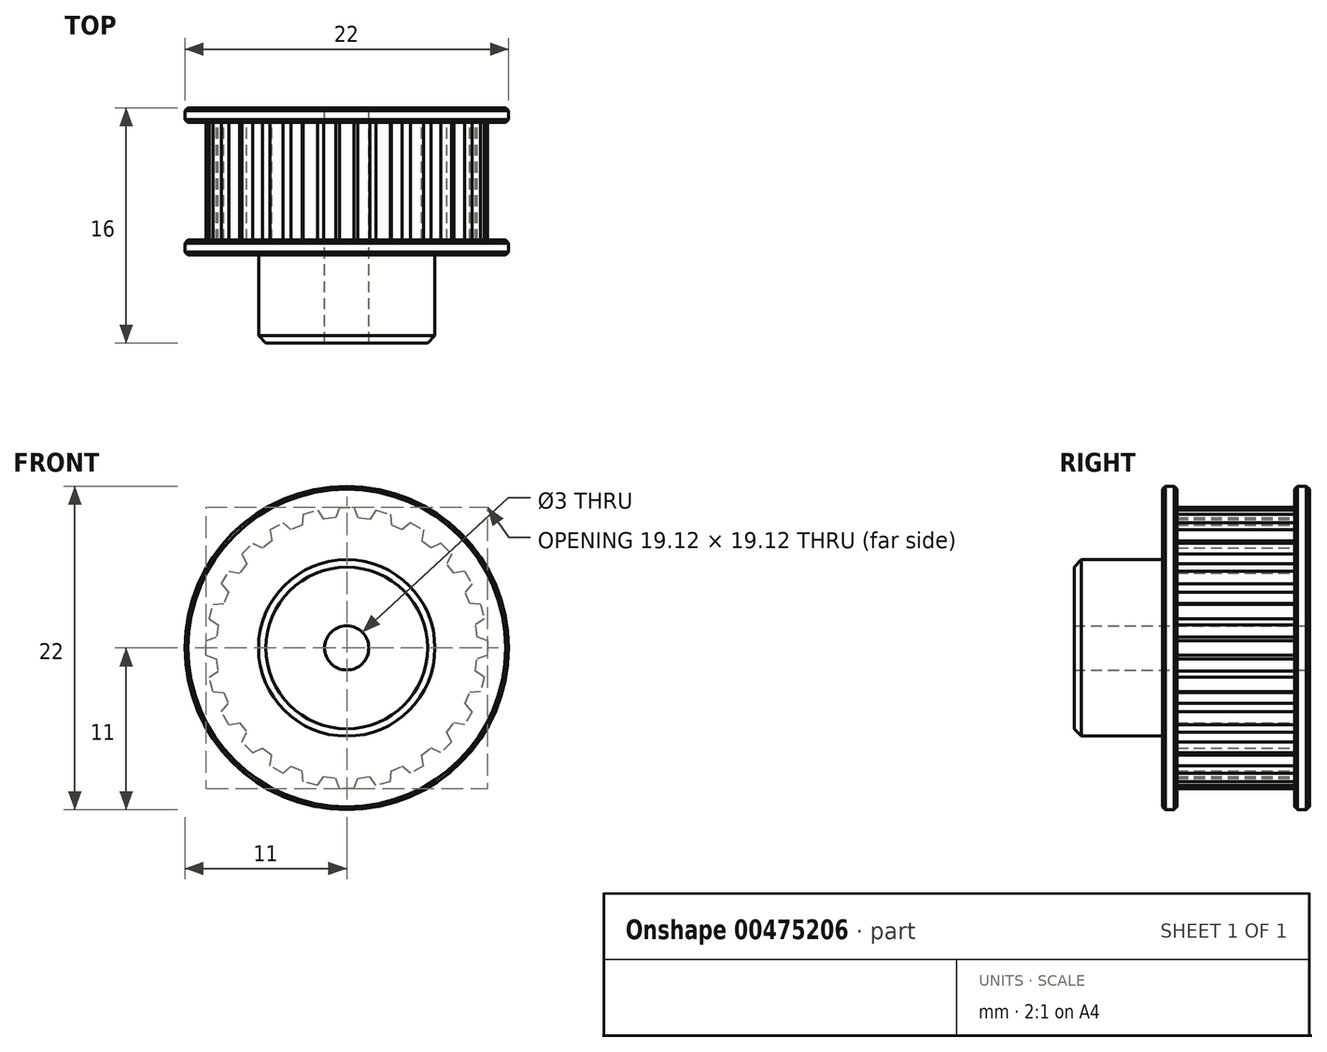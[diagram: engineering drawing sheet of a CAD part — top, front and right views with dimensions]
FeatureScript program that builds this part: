
annotation { "Feature Type Name" : "Feature", "Feature Type Description" : "" }
export const myFeature = defineFeature(function(context is Context, id is Id, definition is map)
    precondition{}
    {
        {
            var Q0;
            Q0=qCreatedBy(makeId("Front.planeOp"),FACE);
            var sketch = newSketch(context, id + "F0", { "sketchPlane" : qUnion([Q0])});
            skCircle(sketch, "E0", {"center": v(0, 0) * mm, "radius": 9.57 * mm, "construction": true});
            skCircle(sketch, "E1", {"center": v(0, 0) * mm, "radius": 6 * mm});
            skLineSegment(sketch, "E2", {"start": v(0, 9.56) * mm, "end": v(-0.5, 9.56) * mm});
            skLineSegment(sketch, "E3", {"start": v(-0.5, 9.56) * mm, "end": v(-0.75, 8.86) * mm});
            skLineSegment(sketch, "E4", {"start": v(-0.75, 8.86) * mm, "end": v(0, 8.86) * mm});
            skLineSegment(sketch, "E5.MirrorCS", {"start": v(0.75, 8.86) * mm, "end": v(0, 8.86) * mm});
            skLineSegment(sketch, "E6.MirrorCS", {"start": v(0, 9.56) * mm, "end": v(0.5, 9.56) * mm});
            skLineSegment(sketch, "E7.MirrorCS", {"start": v(0.5, 9.56) * mm, "end": v(0.75, 8.86) * mm});
            skLineSegment(sketch, "E8.1.0", {"start": v(1.56, 8.76) * mm, "end": v(2.3, 8.56) * mm});
            skLineSegment(sketch, "E8.1.1", {"start": v(3.02, 8.36) * mm, "end": v(2.3, 8.56) * mm});
            skLineSegment(sketch, "E8.1.2", {"start": v(2.96, 9.1) * mm, "end": v(3.02, 8.36) * mm});
            skLineSegment(sketch, "E8.1.3", {"start": v(2, 9.37) * mm, "end": v(1.56, 8.76) * mm});
            skLineSegment(sketch, "E8.1.4", {"start": v(2.47, 9.24) * mm, "end": v(2.96, 9.1) * mm});
            skLineSegment(sketch, "E8.1.5", {"start": v(2.47, 9.24) * mm, "end": v(2, 9.37) * mm});
            skLineSegment(sketch, "E8.2.0", {"start": v(3.78, 8.05) * mm, "end": v(4.43, 7.67) * mm});
            skLineSegment(sketch, "E8.2.1", {"start": v(5.08, 7.3) * mm, "end": v(4.43, 7.67) * mm});
            skLineSegment(sketch, "E8.2.2", {"start": v(5.21, 8.03) * mm, "end": v(5.08, 7.3) * mm});
            skLineSegment(sketch, "E8.2.3", {"start": v(4.35, 8.53) * mm, "end": v(3.78, 8.05) * mm});
            skLineSegment(sketch, "E8.2.4", {"start": v(4.78, 8.28) * mm, "end": v(5.21, 8.03) * mm});
            skLineSegment(sketch, "E8.2.5", {"start": v(4.78, 8.28) * mm, "end": v(4.35, 8.53) * mm});
            skLineSegment(sketch, "E8.3.0", {"start": v(5.73, 6.8) * mm, "end": v(6.27, 6.27) * mm});
            skLineSegment(sketch, "E8.3.1", {"start": v(6.8, 5.73) * mm, "end": v(6.27, 6.27) * mm});
            skLineSegment(sketch, "E8.3.2", {"start": v(7.11, 6.4) * mm, "end": v(6.8, 5.73) * mm});
            skLineSegment(sketch, "E8.3.3", {"start": v(6.4, 7.11) * mm, "end": v(5.73, 6.8) * mm});
            skLineSegment(sketch, "E8.3.4", {"start": v(6.76, 6.76) * mm, "end": v(7.11, 6.4) * mm});
            skLineSegment(sketch, "E8.3.5", {"start": v(6.76, 6.76) * mm, "end": v(6.4, 7.11) * mm});
            skLineSegment(sketch, "E8.4.0", {"start": v(7.3, 5.08) * mm, "end": v(7.67, 4.43) * mm});
            skLineSegment(sketch, "E8.4.1", {"start": v(8.05, 3.78) * mm, "end": v(7.67, 4.43) * mm});
            skLineSegment(sketch, "E8.4.2", {"start": v(8.53, 4.35) * mm, "end": v(8.05, 3.78) * mm});
            skLineSegment(sketch, "E8.4.3", {"start": v(8.03, 5.21) * mm, "end": v(7.3, 5.08) * mm});
            skLineSegment(sketch, "E8.4.4", {"start": v(8.28, 4.78) * mm, "end": v(8.53, 4.35) * mm});
            skLineSegment(sketch, "E8.4.5", {"start": v(8.28, 4.78) * mm, "end": v(8.03, 5.21) * mm});
            skLineSegment(sketch, "E8.5.0", {"start": v(8.36, 3.02) * mm, "end": v(8.56, 2.3) * mm});
            skLineSegment(sketch, "E8.5.1", {"start": v(8.76, 1.56) * mm, "end": v(8.56, 2.3) * mm});
            skLineSegment(sketch, "E8.5.2", {"start": v(9.37, 2) * mm, "end": v(8.76, 1.56) * mm});
            skLineSegment(sketch, "E8.5.3", {"start": v(9.1, 2.96) * mm, "end": v(8.36, 3.02) * mm});
            skLineSegment(sketch, "E8.5.4", {"start": v(9.24, 2.47) * mm, "end": v(9.37, 2) * mm});
            skLineSegment(sketch, "E8.5.5", {"start": v(9.24, 2.47) * mm, "end": v(9.1, 2.96) * mm});
            skLineSegment(sketch, "E8.6.0", {"start": v(8.86, 0.75) * mm, "end": v(8.86, 0) * mm});
            skLineSegment(sketch, "E8.6.1", {"start": v(8.86, -0.75) * mm, "end": v(8.86, 0) * mm});
            skLineSegment(sketch, "E8.6.2", {"start": v(9.56, -0.5) * mm, "end": v(8.86, -0.75) * mm});
            skLineSegment(sketch, "E8.6.3", {"start": v(9.56, 0.5) * mm, "end": v(8.86, 0.75) * mm});
            skLineSegment(sketch, "E8.6.4", {"start": v(9.56, 0) * mm, "end": v(9.56, -0.5) * mm});
            skLineSegment(sketch, "E8.6.5", {"start": v(9.56, 0) * mm, "end": v(9.56, 0.5) * mm});
            skLineSegment(sketch, "E8.7.0", {"start": v(8.76, -1.56) * mm, "end": v(8.56, -2.3) * mm});
            skLineSegment(sketch, "E8.7.1", {"start": v(8.36, -3.02) * mm, "end": v(8.56, -2.3) * mm});
            skLineSegment(sketch, "E8.7.2", {"start": v(9.1, -2.96) * mm, "end": v(8.36, -3.02) * mm});
            skLineSegment(sketch, "E8.7.3", {"start": v(9.37, -2) * mm, "end": v(8.76, -1.56) * mm});
            skLineSegment(sketch, "E8.7.4", {"start": v(9.24, -2.47) * mm, "end": v(9.1, -2.96) * mm});
            skLineSegment(sketch, "E8.7.5", {"start": v(9.24, -2.47) * mm, "end": v(9.37, -2) * mm});
            skLineSegment(sketch, "E8.8.0", {"start": v(8.05, -3.78) * mm, "end": v(7.67, -4.43) * mm});
            skLineSegment(sketch, "E8.8.1", {"start": v(7.3, -5.08) * mm, "end": v(7.67, -4.43) * mm});
            skLineSegment(sketch, "E8.8.2", {"start": v(8.03, -5.21) * mm, "end": v(7.3, -5.08) * mm});
            skLineSegment(sketch, "E8.8.3", {"start": v(8.53, -4.35) * mm, "end": v(8.05, -3.78) * mm});
            skLineSegment(sketch, "E8.8.4", {"start": v(8.28, -4.78) * mm, "end": v(8.03, -5.21) * mm});
            skLineSegment(sketch, "E8.8.5", {"start": v(8.28, -4.78) * mm, "end": v(8.53, -4.35) * mm});
            skLineSegment(sketch, "E8.9.0", {"start": v(6.8, -5.73) * mm, "end": v(6.27, -6.27) * mm});
            skLineSegment(sketch, "E8.9.1", {"start": v(5.73, -6.8) * mm, "end": v(6.27, -6.27) * mm});
            skLineSegment(sketch, "E8.9.2", {"start": v(6.4, -7.11) * mm, "end": v(5.73, -6.8) * mm});
            skLineSegment(sketch, "E8.9.3", {"start": v(7.11, -6.4) * mm, "end": v(6.8, -5.73) * mm});
            skLineSegment(sketch, "E8.9.4", {"start": v(6.76, -6.76) * mm, "end": v(6.4, -7.11) * mm});
            skLineSegment(sketch, "E8.9.5", {"start": v(6.76, -6.76) * mm, "end": v(7.11, -6.4) * mm});
            skLineSegment(sketch, "E8.10.0", {"start": v(5.08, -7.3) * mm, "end": v(4.43, -7.67) * mm});
            skLineSegment(sketch, "E8.10.1", {"start": v(3.78, -8.05) * mm, "end": v(4.43, -7.67) * mm});
            skLineSegment(sketch, "E8.10.2", {"start": v(4.35, -8.53) * mm, "end": v(3.78, -8.05) * mm});
            skLineSegment(sketch, "E8.10.3", {"start": v(5.21, -8.03) * mm, "end": v(5.08, -7.3) * mm});
            skLineSegment(sketch, "E8.10.4", {"start": v(4.78, -8.28) * mm, "end": v(4.35, -8.53) * mm});
            skLineSegment(sketch, "E8.10.5", {"start": v(4.78, -8.28) * mm, "end": v(5.21, -8.03) * mm});
            skLineSegment(sketch, "E8.11.0", {"start": v(3.02, -8.36) * mm, "end": v(2.3, -8.56) * mm});
            skLineSegment(sketch, "E8.11.1", {"start": v(1.56, -8.76) * mm, "end": v(2.3, -8.56) * mm});
            skLineSegment(sketch, "E8.11.2", {"start": v(2, -9.37) * mm, "end": v(1.56, -8.76) * mm});
            skLineSegment(sketch, "E8.11.3", {"start": v(2.96, -9.1) * mm, "end": v(3.02, -8.36) * mm});
            skLineSegment(sketch, "E8.11.4", {"start": v(2.47, -9.24) * mm, "end": v(2, -9.37) * mm});
            skLineSegment(sketch, "E8.11.5", {"start": v(2.47, -9.24) * mm, "end": v(2.96, -9.1) * mm});
            skLineSegment(sketch, "E8.12.0", {"start": v(0.75, -8.86) * mm, "end": v(0, -8.86) * mm});
            skLineSegment(sketch, "E8.12.1", {"start": v(-0.75, -8.86) * mm, "end": v(0, -8.86) * mm});
            skLineSegment(sketch, "E8.12.2", {"start": v(-0.5, -9.56) * mm, "end": v(-0.75, -8.86) * mm});
            skLineSegment(sketch, "E8.12.3", {"start": v(0.5, -9.56) * mm, "end": v(0.75, -8.86) * mm});
            skLineSegment(sketch, "E8.12.4", {"start": v(0, -9.56) * mm, "end": v(-0.5, -9.56) * mm});
            skLineSegment(sketch, "E8.12.5", {"start": v(0, -9.56) * mm, "end": v(0.5, -9.56) * mm});
            skLineSegment(sketch, "E8.13.0", {"start": v(-1.56, -8.76) * mm, "end": v(-2.3, -8.56) * mm});
            skLineSegment(sketch, "E8.13.1", {"start": v(-3.02, -8.36) * mm, "end": v(-2.3, -8.56) * mm});
            skLineSegment(sketch, "E8.13.2", {"start": v(-2.96, -9.1) * mm, "end": v(-3.02, -8.36) * mm});
            skLineSegment(sketch, "E8.13.3", {"start": v(-2, -9.37) * mm, "end": v(-1.56, -8.76) * mm});
            skLineSegment(sketch, "E8.13.4", {"start": v(-2.47, -9.24) * mm, "end": v(-2.96, -9.1) * mm});
            skLineSegment(sketch, "E8.13.5", {"start": v(-2.47, -9.24) * mm, "end": v(-2, -9.37) * mm});
            skLineSegment(sketch, "E8.14.0", {"start": v(-3.78, -8.05) * mm, "end": v(-4.43, -7.67) * mm});
            skLineSegment(sketch, "E8.14.1", {"start": v(-5.08, -7.3) * mm, "end": v(-4.43, -7.67) * mm});
            skLineSegment(sketch, "E8.14.2", {"start": v(-5.21, -8.03) * mm, "end": v(-5.08, -7.3) * mm});
            skLineSegment(sketch, "E8.14.3", {"start": v(-4.35, -8.53) * mm, "end": v(-3.78, -8.05) * mm});
            skLineSegment(sketch, "E8.14.4", {"start": v(-4.78, -8.28) * mm, "end": v(-5.21, -8.03) * mm});
            skLineSegment(sketch, "E8.14.5", {"start": v(-4.78, -8.28) * mm, "end": v(-4.35, -8.53) * mm});
            skLineSegment(sketch, "E8.15.0", {"start": v(-5.73, -6.8) * mm, "end": v(-6.27, -6.27) * mm});
            skLineSegment(sketch, "E8.15.1", {"start": v(-6.8, -5.73) * mm, "end": v(-6.27, -6.27) * mm});
            skLineSegment(sketch, "E8.15.2", {"start": v(-7.11, -6.4) * mm, "end": v(-6.8, -5.73) * mm});
            skLineSegment(sketch, "E8.15.3", {"start": v(-6.4, -7.11) * mm, "end": v(-5.73, -6.8) * mm});
            skLineSegment(sketch, "E8.15.4", {"start": v(-6.76, -6.76) * mm, "end": v(-7.11, -6.4) * mm});
            skLineSegment(sketch, "E8.15.5", {"start": v(-6.76, -6.76) * mm, "end": v(-6.4, -7.11) * mm});
            skLineSegment(sketch, "E8.16.0", {"start": v(-7.3, -5.08) * mm, "end": v(-7.67, -4.43) * mm});
            skLineSegment(sketch, "E8.16.1", {"start": v(-8.05, -3.78) * mm, "end": v(-7.67, -4.43) * mm});
            skLineSegment(sketch, "E8.16.2", {"start": v(-8.53, -4.35) * mm, "end": v(-8.05, -3.78) * mm});
            skLineSegment(sketch, "E8.16.3", {"start": v(-8.03, -5.21) * mm, "end": v(-7.3, -5.08) * mm});
            skLineSegment(sketch, "E8.16.4", {"start": v(-8.28, -4.78) * mm, "end": v(-8.53, -4.35) * mm});
            skLineSegment(sketch, "E8.16.5", {"start": v(-8.28, -4.78) * mm, "end": v(-8.03, -5.21) * mm});
            skLineSegment(sketch, "E8.17.0", {"start": v(-8.36, -3.02) * mm, "end": v(-8.56, -2.3) * mm});
            skLineSegment(sketch, "E8.17.1", {"start": v(-8.76, -1.56) * mm, "end": v(-8.56, -2.3) * mm});
            skLineSegment(sketch, "E8.17.2", {"start": v(-9.37, -2) * mm, "end": v(-8.76, -1.56) * mm});
            skLineSegment(sketch, "E8.17.3", {"start": v(-9.1, -2.96) * mm, "end": v(-8.36, -3.02) * mm});
            skLineSegment(sketch, "E8.17.4", {"start": v(-9.24, -2.47) * mm, "end": v(-9.37, -2) * mm});
            skLineSegment(sketch, "E8.17.5", {"start": v(-9.24, -2.47) * mm, "end": v(-9.1, -2.96) * mm});
            skLineSegment(sketch, "E8.18.0", {"start": v(-8.86, -0.75) * mm, "end": v(-8.86, 0) * mm});
            skLineSegment(sketch, "E8.18.1", {"start": v(-8.86, 0.75) * mm, "end": v(-8.86, 0) * mm});
            skLineSegment(sketch, "E8.18.2", {"start": v(-9.56, 0.5) * mm, "end": v(-8.86, 0.75) * mm});
            skLineSegment(sketch, "E8.18.3", {"start": v(-9.56, -0.5) * mm, "end": v(-8.86, -0.75) * mm});
            skLineSegment(sketch, "E8.18.4", {"start": v(-9.56, 0) * mm, "end": v(-9.56, 0.5) * mm});
            skLineSegment(sketch, "E8.18.5", {"start": v(-9.56, 0) * mm, "end": v(-9.56, -0.5) * mm});
            skLineSegment(sketch, "E8.19.0", {"start": v(-8.76, 1.56) * mm, "end": v(-8.56, 2.3) * mm});
            skLineSegment(sketch, "E8.19.1", {"start": v(-8.36, 3.02) * mm, "end": v(-8.56, 2.3) * mm});
            skLineSegment(sketch, "E8.19.2", {"start": v(-9.1, 2.96) * mm, "end": v(-8.36, 3.02) * mm});
            skLineSegment(sketch, "E8.19.3", {"start": v(-9.37, 2) * mm, "end": v(-8.76, 1.56) * mm});
            skLineSegment(sketch, "E8.19.4", {"start": v(-9.24, 2.47) * mm, "end": v(-9.1, 2.96) * mm});
            skLineSegment(sketch, "E8.19.5", {"start": v(-9.24, 2.47) * mm, "end": v(-9.37, 2) * mm});
            skLineSegment(sketch, "E8.20.0", {"start": v(-8.05, 3.78) * mm, "end": v(-7.67, 4.43) * mm});
            skLineSegment(sketch, "E8.20.1", {"start": v(-7.3, 5.08) * mm, "end": v(-7.67, 4.43) * mm});
            skLineSegment(sketch, "E8.20.2", {"start": v(-8.03, 5.21) * mm, "end": v(-7.3, 5.08) * mm});
            skLineSegment(sketch, "E8.20.3", {"start": v(-8.53, 4.35) * mm, "end": v(-8.05, 3.78) * mm});
            skLineSegment(sketch, "E8.20.4", {"start": v(-8.28, 4.78) * mm, "end": v(-8.03, 5.21) * mm});
            skLineSegment(sketch, "E8.20.5", {"start": v(-8.28, 4.78) * mm, "end": v(-8.53, 4.35) * mm});
            skLineSegment(sketch, "E8.21.0", {"start": v(-6.8, 5.73) * mm, "end": v(-6.27, 6.27) * mm});
            skLineSegment(sketch, "E8.21.1", {"start": v(-5.73, 6.8) * mm, "end": v(-6.27, 6.27) * mm});
            skLineSegment(sketch, "E8.21.2", {"start": v(-6.4, 7.11) * mm, "end": v(-5.73, 6.8) * mm});
            skLineSegment(sketch, "E8.21.3", {"start": v(-7.11, 6.4) * mm, "end": v(-6.8, 5.73) * mm});
            skLineSegment(sketch, "E8.21.4", {"start": v(-6.76, 6.76) * mm, "end": v(-6.4, 7.11) * mm});
            skLineSegment(sketch, "E8.21.5", {"start": v(-6.76, 6.76) * mm, "end": v(-7.11, 6.4) * mm});
            skLineSegment(sketch, "E8.22.0", {"start": v(-5.08, 7.3) * mm, "end": v(-4.43, 7.67) * mm});
            skLineSegment(sketch, "E8.22.1", {"start": v(-3.78, 8.05) * mm, "end": v(-4.43, 7.67) * mm});
            skLineSegment(sketch, "E8.22.2", {"start": v(-4.35, 8.53) * mm, "end": v(-3.78, 8.05) * mm});
            skLineSegment(sketch, "E8.22.3", {"start": v(-5.21, 8.03) * mm, "end": v(-5.08, 7.3) * mm});
            skLineSegment(sketch, "E8.22.4", {"start": v(-4.78, 8.28) * mm, "end": v(-4.35, 8.53) * mm});
            skLineSegment(sketch, "E8.22.5", {"start": v(-4.78, 8.28) * mm, "end": v(-5.21, 8.03) * mm});
            skLineSegment(sketch, "E8.23.0", {"start": v(-3.02, 8.36) * mm, "end": v(-2.3, 8.56) * mm});
            skLineSegment(sketch, "E8.23.1", {"start": v(-1.56, 8.76) * mm, "end": v(-2.3, 8.56) * mm});
            skLineSegment(sketch, "E8.23.2", {"start": v(-2, 9.37) * mm, "end": v(-1.56, 8.76) * mm});
            skLineSegment(sketch, "E8.23.3", {"start": v(-2.96, 9.1) * mm, "end": v(-3.02, 8.36) * mm});
            skLineSegment(sketch, "E8.23.4", {"start": v(-2.47, 9.24) * mm, "end": v(-2, 9.37) * mm});
            skLineSegment(sketch, "E8.23.5", {"start": v(-2.47, 9.24) * mm, "end": v(-2.96, 9.1) * mm});
            skLineSegment(sketch, "E8.anchor1", {"start": v(0, 0) * mm, "end": v(-0.75, 8.86) * mm, "construction": true});
            skLineSegment(sketch, "E8.anchor2", {"start": v(0, 0) * mm, "end": v(-3.02, 8.36) * mm, "construction": true});
            skLineSegment(sketch, "E9", {"start": v(-0.75, 8.86) * mm, "end": v(-1.56, 8.76) * mm});
            skLineSegment(sketch, "E10.1.0", {"start": v(1.56, 8.76) * mm, "end": v(0.75, 8.86) * mm});
            skLineSegment(sketch, "E10.2.0", {"start": v(3.78, 8.05) * mm, "end": v(3.02, 8.36) * mm});
            skLineSegment(sketch, "E10.3.0", {"start": v(5.73, 6.8) * mm, "end": v(5.08, 7.3) * mm});
            skLineSegment(sketch, "E10.4.0", {"start": v(7.3, 5.08) * mm, "end": v(6.8, 5.73) * mm});
            skLineSegment(sketch, "E10.5.0", {"start": v(8.36, 3.02) * mm, "end": v(8.05, 3.78) * mm});
            skLineSegment(sketch, "E10.6.0", {"start": v(8.86, 0.75) * mm, "end": v(8.76, 1.56) * mm});
            skLineSegment(sketch, "E10.7.0", {"start": v(8.76, -1.56) * mm, "end": v(8.86, -0.75) * mm});
            skLineSegment(sketch, "E10.8.0", {"start": v(8.05, -3.78) * mm, "end": v(8.36, -3.02) * mm});
            skLineSegment(sketch, "E10.9.0", {"start": v(6.8, -5.73) * mm, "end": v(7.3, -5.08) * mm});
            skLineSegment(sketch, "E10.10.0", {"start": v(5.08, -7.3) * mm, "end": v(5.73, -6.8) * mm});
            skLineSegment(sketch, "E10.11.0", {"start": v(3.02, -8.36) * mm, "end": v(3.78, -8.05) * mm});
            skLineSegment(sketch, "E10.12.0", {"start": v(0.75, -8.86) * mm, "end": v(1.56, -8.76) * mm});
            skLineSegment(sketch, "E10.13.0", {"start": v(-1.56, -8.76) * mm, "end": v(-0.75, -8.86) * mm});
            skLineSegment(sketch, "E10.14.0", {"start": v(-3.78, -8.05) * mm, "end": v(-3.02, -8.36) * mm});
            skLineSegment(sketch, "E10.15.0", {"start": v(-5.73, -6.8) * mm, "end": v(-5.08, -7.3) * mm});
            skLineSegment(sketch, "E10.16.0", {"start": v(-7.3, -5.08) * mm, "end": v(-6.8, -5.73) * mm});
            skLineSegment(sketch, "E10.17.0", {"start": v(-8.36, -3.02) * mm, "end": v(-8.05, -3.78) * mm});
            skLineSegment(sketch, "E10.18.0", {"start": v(-8.86, -0.75) * mm, "end": v(-8.76, -1.56) * mm});
            skLineSegment(sketch, "E10.19.0", {"start": v(-8.76, 1.56) * mm, "end": v(-8.86, 0.75) * mm});
            skLineSegment(sketch, "E10.20.0", {"start": v(-8.05, 3.78) * mm, "end": v(-8.36, 3.02) * mm});
            skLineSegment(sketch, "E10.21.0", {"start": v(-6.8, 5.73) * mm, "end": v(-7.3, 5.08) * mm});
            skLineSegment(sketch, "E10.22.0", {"start": v(-5.08, 7.3) * mm, "end": v(-5.73, 6.8) * mm});
            skLineSegment(sketch, "E10.23.0", {"start": v(-3.02, 8.36) * mm, "end": v(-3.78, 8.05) * mm});
            skLineSegment(sketch, "E10.anchor1", {"start": v(0, 0) * mm, "end": v(-1.56, 8.76) * mm, "construction": true});
            skLineSegment(sketch, "E10.anchor2", {"start": v(0, 0) * mm, "end": v(-3.78, 8.05) * mm, "construction": true});
            skSolve(sketch);
        }
        {
            var Q0;
            Q0=makeQuery(id+"F0.imprint","IMPRINT",FACE,{"disambiguationData":[TD([[makeQuery(id+"F0.imprint","IMPRINT",EDGE,{"derivedFrom":sQuery(id+"F0.wireOp",EDGE,"E1")}),-1.0]])]});
            var Q1;
            Q1=makeQuery(id+"F0.imprint","IMPRINT",FACE,{"disambiguationData":[TD([[makeQuery(id+"F0.imprint","IMPRINT",EDGE,{"derivedFrom":sQuery(id+"F0.wireOp",EDGE,"E8.22.0")}),1.0]])]});
            var Q2;
            Q2=makeQuery(id+"F0.imprint","IMPRINT",FACE,{"disambiguationData":[TD([[makeQuery(id+"F0.imprint","IMPRINT",EDGE,{"derivedFrom":sQuery(id+"F0.wireOp",EDGE,"E8.21.0")}),1.0]])]});
            var Q3;
            Q3=makeQuery(id+"F0.imprint","IMPRINT",FACE,{"disambiguationData":[TD([[makeQuery(id+"F0.imprint","IMPRINT",EDGE,{"derivedFrom":sQuery(id+"F0.wireOp",EDGE,"E8.20.0")}),1.0]])]});
            var Q4;
            Q4=makeQuery(id+"F0.imprint","IMPRINT",FACE,{"disambiguationData":[TD([[makeQuery(id+"F0.imprint","IMPRINT",EDGE,{"derivedFrom":sQuery(id+"F0.wireOp",EDGE,"E8.19.0")}),1.0]])]});
            var Q5;
            Q5=makeQuery(id+"F0.imprint","IMPRINT",FACE,{"disambiguationData":[TD([[makeQuery(id+"F0.imprint","IMPRINT",EDGE,{"derivedFrom":sQuery(id+"F0.wireOp",EDGE,"E8.18.0")}),1.0]])]});
            var Q6;
            Q6=makeQuery(id+"F0.imprint","IMPRINT",FACE,{"disambiguationData":[TD([[makeQuery(id+"F0.imprint","IMPRINT",EDGE,{"derivedFrom":sQuery(id+"F0.wireOp",EDGE,"E8.17.0")}),1.0]])]});
            var Q7;
            Q7=makeQuery(id+"F0.imprint","IMPRINT",FACE,{"disambiguationData":[TD([[makeQuery(id+"F0.imprint","IMPRINT",EDGE,{"derivedFrom":sQuery(id+"F0.wireOp",EDGE,"E8.16.0")}),1.0]])]});
            var Q8;
            Q8=makeQuery(id+"F0.imprint","IMPRINT",FACE,{"disambiguationData":[TD([[makeQuery(id+"F0.imprint","IMPRINT",EDGE,{"derivedFrom":sQuery(id+"F0.wireOp",EDGE,"E8.15.0")}),1.0]])]});
            var Q9;
            Q9=makeQuery(id+"F0.imprint","IMPRINT",FACE,{"disambiguationData":[TD([[makeQuery(id+"F0.imprint","IMPRINT",EDGE,{"derivedFrom":sQuery(id+"F0.wireOp",EDGE,"E8.14.0")}),1.0]])]});
            var Q10;
            Q10=makeQuery(id+"F0.imprint","IMPRINT",FACE,{"disambiguationData":[TD([[makeQuery(id+"F0.imprint","IMPRINT",EDGE,{"derivedFrom":sQuery(id+"F0.wireOp",EDGE,"E8.13.0")}),1.0]])]});
            var Q11;
            Q11=makeQuery(id+"F0.imprint","IMPRINT",FACE,{"disambiguationData":[TD([[makeQuery(id+"F0.imprint","IMPRINT",EDGE,{"derivedFrom":sQuery(id+"F0.wireOp",EDGE,"E8.12.0")}),1.0]])]});
            var Q12;
            Q12=makeQuery(id+"F0.imprint","IMPRINT",FACE,{"disambiguationData":[TD([[makeQuery(id+"F0.imprint","IMPRINT",EDGE,{"derivedFrom":sQuery(id+"F0.wireOp",EDGE,"E8.11.0")}),1.0]])]});
            var Q13;
            Q13=makeQuery(id+"F0.imprint","IMPRINT",FACE,{"disambiguationData":[TD([[makeQuery(id+"F0.imprint","IMPRINT",EDGE,{"derivedFrom":sQuery(id+"F0.wireOp",EDGE,"E8.10.0")}),1.0]])]});
            var Q14;
            Q14=makeQuery(id+"F0.imprint","IMPRINT",FACE,{"disambiguationData":[TD([[makeQuery(id+"F0.imprint","IMPRINT",EDGE,{"derivedFrom":sQuery(id+"F0.wireOp",EDGE,"E8.9.0")}),1.0]])]});
            var Q15;
            Q15=makeQuery(id+"F0.imprint","IMPRINT",FACE,{"disambiguationData":[TD([[makeQuery(id+"F0.imprint","IMPRINT",EDGE,{"derivedFrom":sQuery(id+"F0.wireOp",EDGE,"E8.8.0")}),1.0]])]});
            var Q16;
            Q16=makeQuery(id+"F0.imprint","IMPRINT",FACE,{"disambiguationData":[TD([[makeQuery(id+"F0.imprint","IMPRINT",EDGE,{"derivedFrom":sQuery(id+"F0.wireOp",EDGE,"E8.7.0")}),1.0]])]});
            var Q17;
            Q17=makeQuery(id+"F0.imprint","IMPRINT",FACE,{"disambiguationData":[TD([[makeQuery(id+"F0.imprint","IMPRINT",EDGE,{"derivedFrom":sQuery(id+"F0.wireOp",EDGE,"E8.6.0")}),1.0]])]});
            var Q18;
            Q18=makeQuery(id+"F0.imprint","IMPRINT",FACE,{"disambiguationData":[TD([[makeQuery(id+"F0.imprint","IMPRINT",EDGE,{"derivedFrom":sQuery(id+"F0.wireOp",EDGE,"E8.5.0")}),1.0]])]});
            var Q19;
            Q19=makeQuery(id+"F0.imprint","IMPRINT",FACE,{"disambiguationData":[TD([[makeQuery(id+"F0.imprint","IMPRINT",EDGE,{"derivedFrom":sQuery(id+"F0.wireOp",EDGE,"E8.4.0")}),1.0]])]});
            var Q20;
            Q20=makeQuery(id+"F0.imprint","IMPRINT",FACE,{"disambiguationData":[TD([[makeQuery(id+"F0.imprint","IMPRINT",EDGE,{"derivedFrom":sQuery(id+"F0.wireOp",EDGE,"E8.3.0")}),1.0]])]});
            var Q21;
            Q21=makeQuery(id+"F0.imprint","IMPRINT",FACE,{"disambiguationData":[TD([[makeQuery(id+"F0.imprint","IMPRINT",EDGE,{"derivedFrom":sQuery(id+"F0.wireOp",EDGE,"E8.2.0")}),1.0]])]});
            var Q22;
            Q22=makeQuery(id+"F0.imprint","IMPRINT",FACE,{"disambiguationData":[TD([[makeQuery(id+"F0.imprint","IMPRINT",EDGE,{"derivedFrom":sQuery(id+"F0.wireOp",EDGE,"E8.1.0")}),1.0]])]});
            var Q23;
            Q23=makeQuery(id+"F0.imprint","IMPRINT",FACE,{"disambiguationData":[TD([[makeQuery(id+"F0.imprint","IMPRINT",EDGE,{"derivedFrom":sQuery(id+"F0.wireOp",EDGE,"E2")}),1.0]])]});
            var Q24;
            Q24=makeQuery(id+"F0.imprint","IMPRINT",FACE,{"disambiguationData":[TD([[makeQuery(id+"F0.imprint","IMPRINT",EDGE,{"derivedFrom":sQuery(id+"F0.wireOp",EDGE,"E8.23.0")}),1.0]])]});
            extrude(context, id + "F1", {"entities" : qUnion([Q0, Q1, Q2, Q3, Q4, Q5, Q6, Q7, Q8, Q9, Q10, Q11, Q12, Q13, Q14, Q15, Q16, Q17, Q18, Q19, Q20, Q21, Q22, Q23, Q24]), "depth" : 10 * mm});
        }
        {
            var Q0;
            Q0=makeQuery(id+"F0.imprint","IMPRINT",FACE,{"disambiguationData":[TD([[makeQuery(id+"F0.imprint","IMPRINT",EDGE,{"derivedFrom":sQuery(id+"F0.wireOp",EDGE,"E1")}),-1.0]])]});
            var sketch = newSketch(context, id + "F2", { "sketchPlane" : qUnion([Q0])});
            skCircle(sketch, "E11", {"center": v(0, 0) * mm, "radius": 11 * mm});
            skSolve(sketch);
        }
        {
            var Q0;
            Q0=makeQuery(id+"F1.opExtrude","CAP_FACE",FACE,{"disambiguationData":[OSD([sQuery(id+"F0.wireOp",EDGE,"E1"),sQuery(id+"F0.wireOp",EDGE,"E2"),sQuery(id+"F0.wireOp",EDGE,"E3"),sQuery(id+"F0.wireOp",EDGE,"E6.MirrorCS"),sQuery(id+"F0.wireOp",EDGE,"E7.MirrorCS"),sQuery(id+"F0.wireOp",EDGE,"E8.1.2"),sQuery(id+"F0.wireOp",EDGE,"E8.1.3"),sQuery(id+"F0.wireOp",EDGE,"E8.1.4"),sQuery(id+"F0.wireOp",EDGE,"E8.1.5"),sQuery(id+"F0.wireOp",EDGE,"E8.2.2"),sQuery(id+"F0.wireOp",EDGE,"E8.2.3"),sQuery(id+"F0.wireOp",EDGE,"E8.2.4"),sQuery(id+"F0.wireOp",EDGE,"E8.2.5"),sQuery(id+"F0.wireOp",EDGE,"E8.3.2"),sQuery(id+"F0.wireOp",EDGE,"E8.3.3"),sQuery(id+"F0.wireOp",EDGE,"E8.3.4"),sQuery(id+"F0.wireOp",EDGE,"E8.3.5"),sQuery(id+"F0.wireOp",EDGE,"E8.4.2"),sQuery(id+"F0.wireOp",EDGE,"E8.4.3"),sQuery(id+"F0.wireOp",EDGE,"E8.4.4"),sQuery(id+"F0.wireOp",EDGE,"E8.4.5"),sQuery(id+"F0.wireOp",EDGE,"E8.5.2"),sQuery(id+"F0.wireOp",EDGE,"E8.5.3"),sQuery(id+"F0.wireOp",EDGE,"E8.5.4"),sQuery(id+"F0.wireOp",EDGE,"E8.5.5"),sQuery(id+"F0.wireOp",EDGE,"E8.6.2"),sQuery(id+"F0.wireOp",EDGE,"E8.6.3"),sQuery(id+"F0.wireOp",EDGE,"E8.6.4"),sQuery(id+"F0.wireOp",EDGE,"E8.6.5"),sQuery(id+"F0.wireOp",EDGE,"E8.7.2"),sQuery(id+"F0.wireOp",EDGE,"E8.7.3"),sQuery(id+"F0.wireOp",EDGE,"E8.7.4"),sQuery(id+"F0.wireOp",EDGE,"E8.7.5"),sQuery(id+"F0.wireOp",EDGE,"E8.8.2"),sQuery(id+"F0.wireOp",EDGE,"E8.8.3"),sQuery(id+"F0.wireOp",EDGE,"E8.8.4"),sQuery(id+"F0.wireOp",EDGE,"E8.8.5"),sQuery(id+"F0.wireOp",EDGE,"E8.9.2"),sQuery(id+"F0.wireOp",EDGE,"E8.9.3"),sQuery(id+"F0.wireOp",EDGE,"E8.9.4"),sQuery(id+"F0.wireOp",EDGE,"E8.9.5"),sQuery(id+"F0.wireOp",EDGE,"E8.10.2"),sQuery(id+"F0.wireOp",EDGE,"E8.10.3"),sQuery(id+"F0.wireOp",EDGE,"E8.10.4"),sQuery(id+"F0.wireOp",EDGE,"E8.10.5"),sQuery(id+"F0.wireOp",EDGE,"E8.11.2"),sQuery(id+"F0.wireOp",EDGE,"E8.11.3"),sQuery(id+"F0.wireOp",EDGE,"E8.11.4"),sQuery(id+"F0.wireOp",EDGE,"E8.11.5"),sQuery(id+"F0.wireOp",EDGE,"E8.12.2"),sQuery(id+"F0.wireOp",EDGE,"E8.12.3"),sQuery(id+"F0.wireOp",EDGE,"E8.12.4"),sQuery(id+"F0.wireOp",EDGE,"E8.12.5"),sQuery(id+"F0.wireOp",EDGE,"E8.13.2"),sQuery(id+"F0.wireOp",EDGE,"E8.13.3"),sQuery(id+"F0.wireOp",EDGE,"E8.13.4"),sQuery(id+"F0.wireOp",EDGE,"E8.13.5"),sQuery(id+"F0.wireOp",EDGE,"E8.14.2"),sQuery(id+"F0.wireOp",EDGE,"E8.14.3"),sQuery(id+"F0.wireOp",EDGE,"E8.14.4"),sQuery(id+"F0.wireOp",EDGE,"E8.14.5"),sQuery(id+"F0.wireOp",EDGE,"E8.15.2"),sQuery(id+"F0.wireOp",EDGE,"E8.15.3"),sQuery(id+"F0.wireOp",EDGE,"E8.15.4"),sQuery(id+"F0.wireOp",EDGE,"E8.15.5"),sQuery(id+"F0.wireOp",EDGE,"E8.16.2"),sQuery(id+"F0.wireOp",EDGE,"E8.16.3"),sQuery(id+"F0.wireOp",EDGE,"E8.16.4"),sQuery(id+"F0.wireOp",EDGE,"E8.16.5"),sQuery(id+"F0.wireOp",EDGE,"E8.17.2"),sQuery(id+"F0.wireOp",EDGE,"E8.17.3"),sQuery(id+"F0.wireOp",EDGE,"E8.17.4"),sQuery(id+"F0.wireOp",EDGE,"E8.17.5"),sQuery(id+"F0.wireOp",EDGE,"E8.18.2"),sQuery(id+"F0.wireOp",EDGE,"E8.18.3"),sQuery(id+"F0.wireOp",EDGE,"E8.18.4"),sQuery(id+"F0.wireOp",EDGE,"E8.18.5"),sQuery(id+"F0.wireOp",EDGE,"E8.19.2"),sQuery(id+"F0.wireOp",EDGE,"E8.19.3"),sQuery(id+"F0.wireOp",EDGE,"E8.19.4"),sQuery(id+"F0.wireOp",EDGE,"E8.19.5"),sQuery(id+"F0.wireOp",EDGE,"E8.20.2"),sQuery(id+"F0.wireOp",EDGE,"E8.20.3"),sQuery(id+"F0.wireOp",EDGE,"E8.20.4"),sQuery(id+"F0.wireOp",EDGE,"E8.20.5"),sQuery(id+"F0.wireOp",EDGE,"E8.21.2"),sQuery(id+"F0.wireOp",EDGE,"E8.21.3"),sQuery(id+"F0.wireOp",EDGE,"E8.21.4"),sQuery(id+"F0.wireOp",EDGE,"E8.21.5"),sQuery(id+"F0.wireOp",EDGE,"E8.22.2"),sQuery(id+"F0.wireOp",EDGE,"E8.22.3"),sQuery(id+"F0.wireOp",EDGE,"E8.22.4"),sQuery(id+"F0.wireOp",EDGE,"E8.22.5"),sQuery(id+"F0.wireOp",EDGE,"E8.23.2"),sQuery(id+"F0.wireOp",EDGE,"E8.23.3"),sQuery(id+"F0.wireOp",EDGE,"E8.23.4"),sQuery(id+"F0.wireOp",EDGE,"E8.23.5"),sQuery(id+"F0.wireOp",EDGE,"E9"),sQuery(id+"F0.wireOp",EDGE,"E10.1.0"),sQuery(id+"F0.wireOp",EDGE,"E10.2.0"),sQuery(id+"F0.wireOp",EDGE,"E10.3.0"),sQuery(id+"F0.wireOp",EDGE,"E10.4.0"),sQuery(id+"F0.wireOp",EDGE,"E10.5.0"),sQuery(id+"F0.wireOp",EDGE,"E10.6.0"),sQuery(id+"F0.wireOp",EDGE,"E10.7.0"),sQuery(id+"F0.wireOp",EDGE,"E10.8.0"),sQuery(id+"F0.wireOp",EDGE,"E10.9.0"),sQuery(id+"F0.wireOp",EDGE,"E10.10.0"),sQuery(id+"F0.wireOp",EDGE,"E10.11.0"),sQuery(id+"F0.wireOp",EDGE,"E10.12.0"),sQuery(id+"F0.wireOp",EDGE,"E10.13.0"),sQuery(id+"F0.wireOp",EDGE,"E10.14.0"),sQuery(id+"F0.wireOp",EDGE,"E10.15.0"),sQuery(id+"F0.wireOp",EDGE,"E10.16.0"),sQuery(id+"F0.wireOp",EDGE,"E10.17.0"),sQuery(id+"F0.wireOp",EDGE,"E10.18.0"),sQuery(id+"F0.wireOp",EDGE,"E10.19.0"),sQuery(id+"F0.wireOp",EDGE,"E10.20.0"),sQuery(id+"F0.wireOp",EDGE,"E10.21.0"),sQuery(id+"F0.wireOp",EDGE,"E10.22.0"),sQuery(id+"F0.wireOp",EDGE,"E10.23.0")])],"isStart":false});
            var sketch = newSketch(context, id + "F3", { "sketchPlane" : qUnion([Q0])});
            skCircle(sketch, "E12", {"center": v(0, 0) * mm, "radius": 11 * mm});
            skSolve(sketch);
        }
        {
            var Q0;
            Q0=makeQuery(id+"F2.imprint","IMPRINT",FACE,{"disambiguationData":[TD([[makeQuery(id+"F2.imprint","IMPRINT",EDGE,{"derivedFrom":sQuery(id+"F2.wireOp",EDGE,"E11")}),1.0]])]});
            extrude(context, id + "F4", {"entities" : qUnion([Q0]), "operationType" : NewBodyOperationType.ADD, "depth" : 1 * mm});
        }
        {
            var Q0;
            Q0=makeQuery(id+"F3.imprint","IMPRINT",FACE,{"disambiguationData":[TD([[makeQuery(id+"F3.imprint","IMPRINT",EDGE,{"derivedFrom":sQuery(id+"F3.wireOp",EDGE,"E12")}),1.0]])]});
            extrude(context, id + "F5", {"entities" : qUnion([Q0]), "operationType" : NewBodyOperationType.ADD, "oppositeDirection" : true, "depth" : 1 * mm});
        }
        {
            var Q0;
            Q0=makeQuery(id+"F0.imprint","IMPRINT",FACE,{"disambiguationData":[TD([[makeQuery(id+"F0.imprint","IMPRINT",EDGE,{"derivedFrom":sQuery(id+"F0.wireOp",EDGE,"E1")}),1.0]])]});
            extrude(context, id + "F6", {"entities" : qUnion([Q0]), "operationType" : NewBodyOperationType.ADD, "depth" : 16 * mm});
        }
        {
            var Q0;
            Q0=sQuery(id+"F0.wireOp",VERTEX,"E0.center");
            var Q1;
            Q1=makeQuery(id+"F1.opExtrude","SWEPT_BODY",BODY,{"disambiguationData":[OSD([sQuery(id+"F0.wireOp",EDGE,"E1"),sQuery(id+"F0.wireOp",EDGE,"E2"),sQuery(id+"F0.wireOp",EDGE,"E3"),sQuery(id+"F0.wireOp",EDGE,"E6.MirrorCS"),sQuery(id+"F0.wireOp",EDGE,"E7.MirrorCS"),sQuery(id+"F0.wireOp",EDGE,"E8.1.2"),sQuery(id+"F0.wireOp",EDGE,"E8.1.3"),sQuery(id+"F0.wireOp",EDGE,"E8.1.4"),sQuery(id+"F0.wireOp",EDGE,"E8.1.5"),sQuery(id+"F0.wireOp",EDGE,"E8.2.2"),sQuery(id+"F0.wireOp",EDGE,"E8.2.3"),sQuery(id+"F0.wireOp",EDGE,"E8.2.4"),sQuery(id+"F0.wireOp",EDGE,"E8.2.5"),sQuery(id+"F0.wireOp",EDGE,"E8.3.2"),sQuery(id+"F0.wireOp",EDGE,"E8.3.3"),sQuery(id+"F0.wireOp",EDGE,"E8.3.4"),sQuery(id+"F0.wireOp",EDGE,"E8.3.5"),sQuery(id+"F0.wireOp",EDGE,"E8.4.2"),sQuery(id+"F0.wireOp",EDGE,"E8.4.3"),sQuery(id+"F0.wireOp",EDGE,"E8.4.4"),sQuery(id+"F0.wireOp",EDGE,"E8.4.5"),sQuery(id+"F0.wireOp",EDGE,"E8.5.2"),sQuery(id+"F0.wireOp",EDGE,"E8.5.3"),sQuery(id+"F0.wireOp",EDGE,"E8.5.4"),sQuery(id+"F0.wireOp",EDGE,"E8.5.5"),sQuery(id+"F0.wireOp",EDGE,"E8.6.2"),sQuery(id+"F0.wireOp",EDGE,"E8.6.3"),sQuery(id+"F0.wireOp",EDGE,"E8.6.4"),sQuery(id+"F0.wireOp",EDGE,"E8.6.5"),sQuery(id+"F0.wireOp",EDGE,"E8.7.2"),sQuery(id+"F0.wireOp",EDGE,"E8.7.3"),sQuery(id+"F0.wireOp",EDGE,"E8.7.4"),sQuery(id+"F0.wireOp",EDGE,"E8.7.5"),sQuery(id+"F0.wireOp",EDGE,"E8.8.2"),sQuery(id+"F0.wireOp",EDGE,"E8.8.3"),sQuery(id+"F0.wireOp",EDGE,"E8.8.4"),sQuery(id+"F0.wireOp",EDGE,"E8.8.5"),sQuery(id+"F0.wireOp",EDGE,"E8.9.2"),sQuery(id+"F0.wireOp",EDGE,"E8.9.3"),sQuery(id+"F0.wireOp",EDGE,"E8.9.4"),sQuery(id+"F0.wireOp",EDGE,"E8.9.5"),sQuery(id+"F0.wireOp",EDGE,"E8.10.2"),sQuery(id+"F0.wireOp",EDGE,"E8.10.3"),sQuery(id+"F0.wireOp",EDGE,"E8.10.4"),sQuery(id+"F0.wireOp",EDGE,"E8.10.5"),sQuery(id+"F0.wireOp",EDGE,"E8.11.2"),sQuery(id+"F0.wireOp",EDGE,"E8.11.3"),sQuery(id+"F0.wireOp",EDGE,"E8.11.4"),sQuery(id+"F0.wireOp",EDGE,"E8.11.5"),sQuery(id+"F0.wireOp",EDGE,"E8.12.2"),sQuery(id+"F0.wireOp",EDGE,"E8.12.3"),sQuery(id+"F0.wireOp",EDGE,"E8.12.4"),sQuery(id+"F0.wireOp",EDGE,"E8.12.5"),sQuery(id+"F0.wireOp",EDGE,"E8.13.2"),sQuery(id+"F0.wireOp",EDGE,"E8.13.3"),sQuery(id+"F0.wireOp",EDGE,"E8.13.4"),sQuery(id+"F0.wireOp",EDGE,"E8.13.5"),sQuery(id+"F0.wireOp",EDGE,"E8.14.2"),sQuery(id+"F0.wireOp",EDGE,"E8.14.3"),sQuery(id+"F0.wireOp",EDGE,"E8.14.4"),sQuery(id+"F0.wireOp",EDGE,"E8.14.5"),sQuery(id+"F0.wireOp",EDGE,"E8.15.2"),sQuery(id+"F0.wireOp",EDGE,"E8.15.3"),sQuery(id+"F0.wireOp",EDGE,"E8.15.4"),sQuery(id+"F0.wireOp",EDGE,"E8.15.5"),sQuery(id+"F0.wireOp",EDGE,"E8.16.2"),sQuery(id+"F0.wireOp",EDGE,"E8.16.3"),sQuery(id+"F0.wireOp",EDGE,"E8.16.4"),sQuery(id+"F0.wireOp",EDGE,"E8.16.5"),sQuery(id+"F0.wireOp",EDGE,"E8.17.2"),sQuery(id+"F0.wireOp",EDGE,"E8.17.3"),sQuery(id+"F0.wireOp",EDGE,"E8.17.4"),sQuery(id+"F0.wireOp",EDGE,"E8.17.5"),sQuery(id+"F0.wireOp",EDGE,"E8.18.2"),sQuery(id+"F0.wireOp",EDGE,"E8.18.3"),sQuery(id+"F0.wireOp",EDGE,"E8.18.4"),sQuery(id+"F0.wireOp",EDGE,"E8.18.5"),sQuery(id+"F0.wireOp",EDGE,"E8.19.2"),sQuery(id+"F0.wireOp",EDGE,"E8.19.3"),sQuery(id+"F0.wireOp",EDGE,"E8.19.4"),sQuery(id+"F0.wireOp",EDGE,"E8.19.5"),sQuery(id+"F0.wireOp",EDGE,"E8.20.2"),sQuery(id+"F0.wireOp",EDGE,"E8.20.3"),sQuery(id+"F0.wireOp",EDGE,"E8.20.4"),sQuery(id+"F0.wireOp",EDGE,"E8.20.5"),sQuery(id+"F0.wireOp",EDGE,"E8.21.2"),sQuery(id+"F0.wireOp",EDGE,"E8.21.3"),sQuery(id+"F0.wireOp",EDGE,"E8.21.4"),sQuery(id+"F0.wireOp",EDGE,"E8.21.5"),sQuery(id+"F0.wireOp",EDGE,"E8.22.2"),sQuery(id+"F0.wireOp",EDGE,"E8.22.3"),sQuery(id+"F0.wireOp",EDGE,"E8.22.4"),sQuery(id+"F0.wireOp",EDGE,"E8.22.5"),sQuery(id+"F0.wireOp",EDGE,"E8.23.2"),sQuery(id+"F0.wireOp",EDGE,"E8.23.3"),sQuery(id+"F0.wireOp",EDGE,"E8.23.4"),sQuery(id+"F0.wireOp",EDGE,"E8.23.5"),sQuery(id+"F0.wireOp",EDGE,"E9"),sQuery(id+"F0.wireOp",EDGE,"E10.1.0"),sQuery(id+"F0.wireOp",EDGE,"E10.2.0"),sQuery(id+"F0.wireOp",EDGE,"E10.3.0"),sQuery(id+"F0.wireOp",EDGE,"E10.4.0"),sQuery(id+"F0.wireOp",EDGE,"E10.5.0"),sQuery(id+"F0.wireOp",EDGE,"E10.6.0"),sQuery(id+"F0.wireOp",EDGE,"E10.7.0"),sQuery(id+"F0.wireOp",EDGE,"E10.8.0"),sQuery(id+"F0.wireOp",EDGE,"E10.9.0"),sQuery(id+"F0.wireOp",EDGE,"E10.10.0"),sQuery(id+"F0.wireOp",EDGE,"E10.11.0"),sQuery(id+"F0.wireOp",EDGE,"E10.12.0"),sQuery(id+"F0.wireOp",EDGE,"E10.13.0"),sQuery(id+"F0.wireOp",EDGE,"E10.14.0"),sQuery(id+"F0.wireOp",EDGE,"E10.15.0"),sQuery(id+"F0.wireOp",EDGE,"E10.16.0"),sQuery(id+"F0.wireOp",EDGE,"E10.17.0"),sQuery(id+"F0.wireOp",EDGE,"E10.18.0"),sQuery(id+"F0.wireOp",EDGE,"E10.19.0"),sQuery(id+"F0.wireOp",EDGE,"E10.20.0"),sQuery(id+"F0.wireOp",EDGE,"E10.21.0"),sQuery(id+"F0.wireOp",EDGE,"E10.22.0"),sQuery(id+"F0.wireOp",EDGE,"E10.23.0")])]});
            hole(context, id + "F7", {"style" : HoleStyle.SIMPLE, "endStyle" : HoleEndStyle.THROUGH, "oppositeDirection" : true, "holeDiameter" : 3 * mm, "isTappedThrough" : true, "tappedDepth" : 12 * mm, "tapClearance" : 3, "locations" : qUnion([Q0]), "scope" : qUnion([Q1])});
        }
        {
            var Q0;
            Q0=makeQuery(id+"F4.opExtrude","CAP_EDGE",EDGE,{"disambiguationData":[OSD([sQuery(id+"F2.wireOp",EDGE,"E11")])],"isStart":true});
            var Q1;
            Q1=makeQuery(id+"F4.opExtrude","CAP_EDGE",EDGE,{"disambiguationData":[OSD([sQuery(id+"F2.wireOp",EDGE,"E11")])],"isStart":false});
            var Q2;
            Q2=makeQuery(id+"F5.opExtrude","CAP_EDGE",EDGE,{"disambiguationData":[OSD([sQuery(id+"F3.wireOp",EDGE,"E12")])],"isStart":false});
            var Q3;
            Q3=makeQuery(id+"F5.opExtrude","CAP_EDGE",EDGE,{"disambiguationData":[OSD([sQuery(id+"F3.wireOp",EDGE,"E12")])],"isStart":true});
            chamfer(context, id + "F8", {"entities" : qUnion([Q0, Q1, Q2, Q3]), "width" : 0.2 * mm, "tangentPropagation" : true});
        }
        {
            var Q0;
            Q0=makeQuery(id+"F6.opExtrude","CAP_EDGE",EDGE,{"disambiguationData":[OSD([sQuery(id+"F0.wireOp",EDGE,"E1")])],"isStart":false});
            var Q1;
            Q1=makeQuery(id+"F7.hole-0.boolean.opBoolean","INTERSECT",EDGE,{"derivedFrom":[makeQuery(id+"F6.opExtrude","CAP_FACE",FACE,{"disambiguationData":[OSD([sQuery(id+"F0.wireOp",EDGE,"E1")])],"isStart":false}),makeQuery(id+"F7.hole-0.opRevolve","SWEPT_FACE",FACE,{"disambiguationData":[OSD([sQuery(id+"F7.hole-0.sketch.wireOp",EDGE,"core_line_2")])]})]});
            var Q2;
            Q2=makeQuery(id+"F7.hole-0.boolean.opBoolean","COPY",EDGE,{"derivedFrom":makeQuery(id+"F7.hole-0.opRevolve","SWEPT_EDGE",EDGE,{"disambiguationData":[OSD([sQuery(id+"F7.hole-0.sketch.wireOp",EDGE,"core_line_2"),sQuery(id+"F7.hole-0.sketch.wireOp",EDGE,"core_line_3")])]})});
            chamfer(context, id + "F9", {"entities" : qUnion([Q0, Q1, Q2]), "width" : 0.5 * mm, "tangentPropagation" : true});
        }
    });
